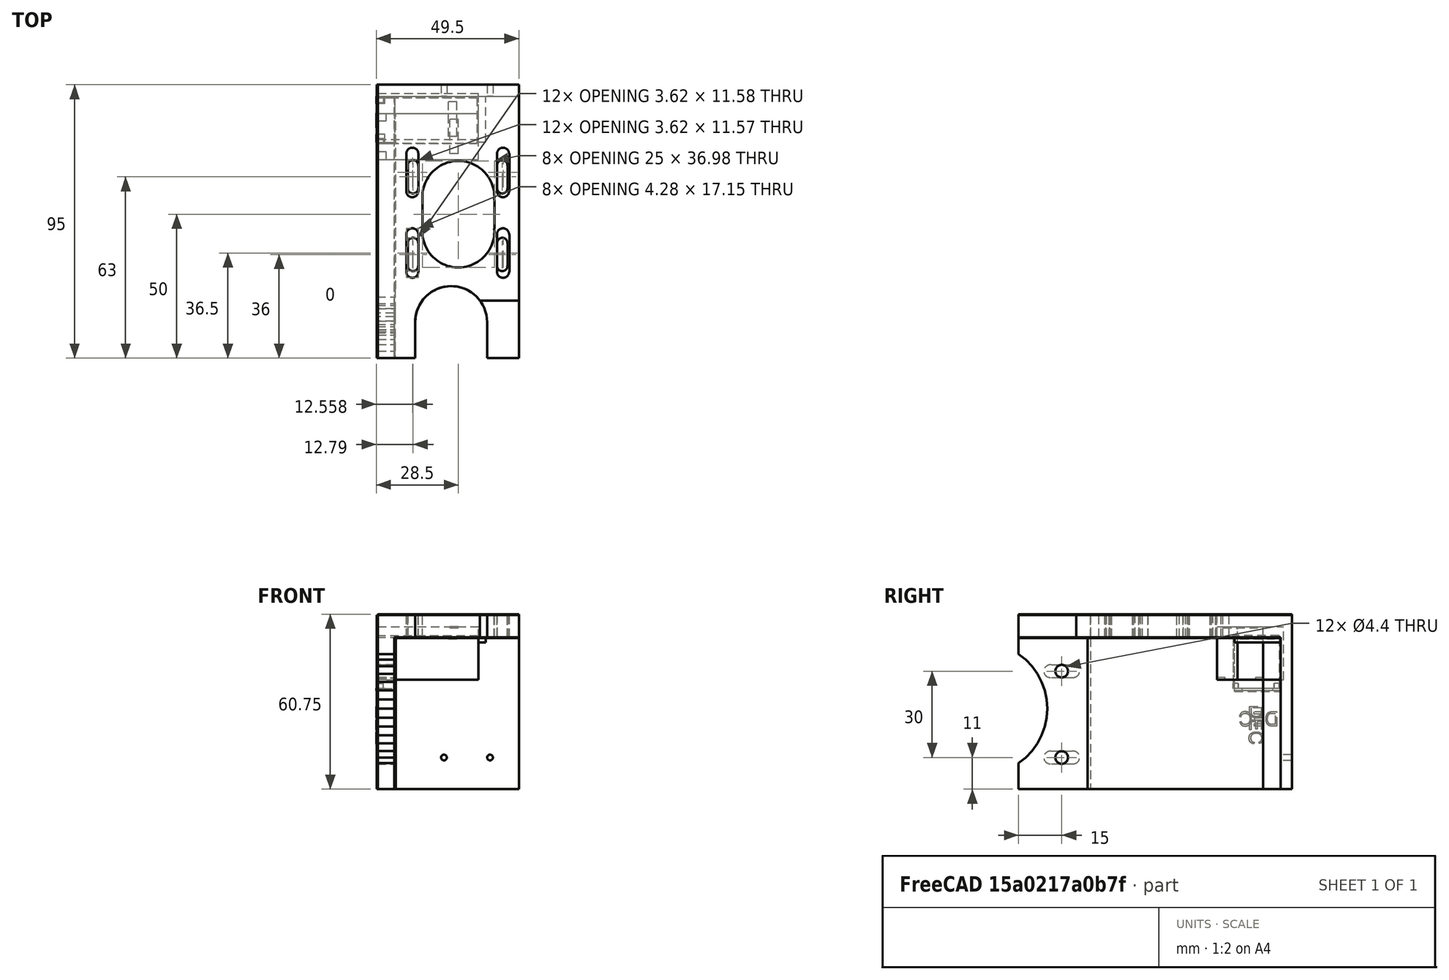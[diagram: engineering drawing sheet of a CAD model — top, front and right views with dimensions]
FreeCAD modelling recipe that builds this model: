
FCSTD DOCUMENT  (FreeCAD 0.17R11223 (Git))
Label: EQ motor V3 fin
License: All rights reserved
LicenseURL: http://en.wikipedia.org/wiki/All_rights_reserved
objects: Part::Feature×18, Part::Box×15, Part::Cut×13, Part::MultiFuse×8, Part::Cylinder×8, Part::Extrusion×3, Part::Part2DObjectPython×1
note: 66 computed .brp shape members not serialized (recipe doc carries the construction recipe); baked Part::Feature solids carry a one-line shape summary decoded from their .brp

FEATURE [Part::Feature] Cut026_solid  label="zadni stena (Solid)"
  shape: bbox 49 x 4 x 60.5 mm, 8 faces (baked)
FEATURE [Part::Feature] Fusion008_solid  label="Boky"
  shape: bbox 49 x 85 x 60.5 mm, 76 faces (baked)
FEATURE [Part::Box] Box005009  label="Krychle009"
  AttacherType = Attacher::AttachEngine3D
  Height = 18.5
  Length = 35
  Placement = pos=(-5,75,-44) rot=(0,0,1;0rad)
  Width = 16
FEATURE [Part::Box] Box005011  label="Krychle010"
  AttacherType = Attacher::AttachEngine3D
  Height = 2.7
  Length = 3
  Placement = pos=(-5,75,-45.8) rot=(0,0,1;0rad)
  Width = 2.7
FEATURE [Part::Box] Box005012  label="Krychle011"
  AttacherType = Attacher::AttachEngine3D
  Height = 2.7
  Length = 3
  Placement = pos=(-5,88.4,-45.8) rot=(0,0,1;0rad)
  Width = 2.7
FEATURE [Part::Box] Box005014  label="Krychle013"
  AttacherType = Attacher::AttachEngine3D
  Height = 2
  Length = 3
  Placement = pos=(20,77,-26) rot=(0,0,1;0rad)
  Width = 12
FEATURE [Part::Box] Box005015  label="Pro RJ"
  AttacherType = Attacher::AttachEngine3D
  Height = 18.5
  Length = 35
  Placement = pos=(-5,82,-44) rot=(0,0,1;0rad)
  Width = 16
FEATURE [Part::Box] Box005016  label="Krychle014"
  AttacherType = Attacher::AttachEngine3D
  Height = 8
  Length = 49
  Placement = pos=(-5,91,-29.5) rot=(0,0,1;0rad)
  Width = 6
FEATURE [Part::Box] Box005017  label="Krychle015"
  AttacherType = Attacher::AttachEngine3D
  Height = 60
  Length = 6
  Placement = pos=(-5,91,-82) rot=(0,0,1;0rad)
  Width = 6
FEATURE [Part::MultiFuse] Fusion
  Shapes = -> [Box005017,Box005016,Cut026_solid,Fusion008_solid]
FEATURE [Part::Feature] Fusion_solid  label="Fusion (Solid)"
  shape: bbox 49 x 95 x 60.5 mm, 91 faces (baked)
FEATURE [Part::Feature] Fusion_solid001  label="Fusion (Solid)001"
  shape: bbox 49 x 95 x 60.5 mm, 72 faces (baked)
FEATURE [Part::Feature] Fusion_solid_cs  label="REZ A"
  shape: bbox 49 x 95 x 4e-07 mm, 0 faces, 0 solids (baked)
FEATURE [Part::Feature] Fusion_solid001_cs  label="REZ B"
  shape: bbox 5e-07 x 95 x 60.5 mm, 0 faces, 0 solids (baked)
FEATURE [Part::Feature] Cut026_solid001  label="zadni stena (Solid)001"
  shape: bbox 49 x 4 x 60.5 mm, 8 faces (baked)
FEATURE [Part::Extrusion] Extrude  label="Vrsek"
  Base = -> Fusion_solid_cs
  Dir = (0,0,1)
  DirMode = 2
  FaceMakerClass = Part::FaceMakerBullseye
  LengthFwd = 8
  LengthRev = 0
  Placement = pos=(0,0,-2.5) rot=(0,0,1;0rad)
  Solid = true
  Symmetric = false
FEATURE [Part::Extrusion] Extrude001  label="Bok"
  Base = -> Fusion_solid001_cs
  Dir = (1,0,0)
  DirMode = 2
  FaceMakerClass = Part::FaceMakerBullseye
  LengthFwd = 6
  LengthRev = 0
  Placement = pos=(-1.8,0,0) rot=(0,0,1;0rad)
  Solid = true
  Symmetric = false
FEATURE [Part::MultiFuse] Fusion001
  Shapes = -> [Cut026_solid001,Extrude,Extrude001]
FEATURE [Part::Feature] Fusion001001  label="Fusion002"
  shape: bbox 49.3 x 95 x 60.75 mm, 66 faces (baked)
FEATURE [Part::Feature] Fusion001001_solid  label="Drzak Bez RJ"
  shape: bbox 49.3 x 95 x 60.75 mm, 66 faces (baked)
FEATURE [Part::Box] Box005018  label="Krychle016"
  AttacherType = Attacher::AttachEngine3D
  Height = 18.5
  Length = 35
  Placement = pos=(-5.5,81,-47.75) rot=(0,0,1;0rad)
  Width = 16
FEATURE [Part::Cut] Cut
  Base = -> Box005009
  Tool = -> Box005011
FEATURE [Part::Cut] Cut001
  Base = -> Cut
  Tool = -> Box005012
FEATURE [Part::Cut] Cut002  label="Pro RJ001"
  Base = -> Cut001
  Tool = -> Box005014
FEATURE [Part::Feature] Cut002_solid  label="Pro RJ001 (Solid)"
  Placement = pos=(-0.5,6,-3.75) rot=(0,0,1;0rad)
  shape: bbox 35 x 16 x 18.5 mm, 17 faces (baked)
FEATURE [Part::MultiFuse] Fusion001002
  Shapes = -> [Fusion001001_solid,Box005018]
FEATURE [Part::Cut] Cut003
  Base = -> Fusion001002
  Tool = -> Cut002_solid
FEATURE [Part::Feature] Cut003001  label="Cut004"
  shape: bbox 49.5 x 95 x 60.75 mm, 85 faces (baked)
FEATURE [Part::Feature] Cut003001_solid  label="EQ motor V3"
  shape: bbox 49.5 x 95 x 60.75 mm, 85 faces (baked)
FEATURE [Part::Box] Box009  label="Doraz003"
  AttacherType = Attacher::AttachEngine3D
  Height = 2
  Length = 2.5
  Placement = pos=(30,81,-31) rot=(0,0,1;0rad)
  Width = 16
FEATURE [Part::Feature] Fusion001003001  label="DIRA 010"
  shape: bbox 8 x 12.4 x 4.5 mm, 10 faces (baked)
FEATURE [Part::Feature] Fusion001003002  label="DIRA 011"
  Placement = pos=(0,0,-30) rot=(0,0,1;0rad)
  shape: bbox 8 x 12.4 x 4.5 mm, 10 faces (baked)
FEATURE [Part::Feature] Cut005_solid002002005  label="RJ45 M DE002"
  Placement = pos=(53.5,165.5,-34) rot=(1,0,0;3.14159rad)
  shape: bbox 35 x 15.95 x 18.45 mm, 12 faces (baked)
FEATURE [Part::Box] Box  label="Krychle"
  AttacherType = Attacher::AttachEngine3D
  Height = 20
  Length = 6.05
  Placement = pos=(-5.2,81,-48) rot=(0,0,1;0rad)
  Width = 16
FEATURE [Part::MultiFuse] Fusion001003003
  Shapes = -> [Box009,Box,Cut003001_solid]
FEATURE [Part::Cut] Cut003002  label="RJ n"
  Base = -> Fusion001003003
  Tool = -> Cut005_solid002002005
FEATURE [Part::Cylinder] Cylinder  label="Válec"
  Angle = 360
  AttacherType = Attacher::AttachEngine3D
  Height = 10
  Radius = 2.1
FEATURE [Part::Cylinder] Cylinder001  label="Válec001"
  Angle = 360
  AttacherType = Attacher::AttachEngine3D
  Height = 10
  Placement = pos=(0,13,0) rot=(0,0,1;0rad)
  Radius = 2.1
FEATURE [Part::Box] Box005019  label="Krychle017"
  AttacherType = Attacher::AttachEngine3D
  Height = 10
  Length = 4.2
  Placement = pos=(-2,0,0) rot=(0,0,1;0rad)
  Width = 13
FEATURE [Part::MultiFuse] Fusion001003004  label="Dira M"
  Placement = pos=(7,36,-30) rot=(0,0,1;0rad)
  Shapes = -> [Cylinder,Cylinder001,Box005019]
FEATURE [Part::Cylinder] Cylinder002  label="Válec002"
  Angle = 360
  AttacherType = Attacher::AttachEngine3D
  Height = 10
  Radius = 2.1
FEATURE [Part::Cylinder] Cylinder003  label="Válec003"
  Angle = 360
  AttacherType = Attacher::AttachEngine3D
  Height = 10
  Placement = pos=(0,13,0) rot=(0,0,1;0rad)
  Radius = 2.1
FEATURE [Part::Box] Box005020  label="Krychle018"
  AttacherType = Attacher::AttachEngine3D
  Height = 10
  Length = 4.2
  Placement = pos=(-2,0,0) rot=(0,0,1;0rad)
  Width = 13
FEATURE [Part::MultiFuse] Fusion001003005  label="Dira M001"
  Placement = pos=(38.5,36,-30) rot=(0,0,1;0rad)
  Shapes = -> [Cylinder002,Cylinder003,Box005020]
FEATURE [Part::Cylinder] Cylinder004  label="Válec004"
  Angle = 360
  AttacherType = Attacher::AttachEngine3D
  Height = 10
  Radius = 2.1
FEATURE [Part::Cylinder] Cylinder005  label="Válec005"
  Angle = 360
  AttacherType = Attacher::AttachEngine3D
  Height = 10
  Placement = pos=(0,13,0) rot=(0,0,1;0rad)
  Radius = 2.1
FEATURE [Part::Box] Box005021  label="Krychle019"
  AttacherType = Attacher::AttachEngine3D
  Height = 10
  Length = 4.2
  Placement = pos=(-2,0,0) rot=(0,0,1;0rad)
  Width = 13
FEATURE [Part::MultiFuse] Fusion001003006  label="Dira M002"
  Placement = pos=(7,64,-30) rot=(0,0,1;0rad)
  Shapes = -> [Cylinder004,Cylinder005,Box005021]
FEATURE [Part::Cylinder] Cylinder006  label="Válec006"
  Angle = 360
  AttacherType = Attacher::AttachEngine3D
  Height = 10
  Radius = 2.1
FEATURE [Part::Cylinder] Cylinder007  label="Válec007"
  Angle = 360
  AttacherType = Attacher::AttachEngine3D
  Height = 10
  Placement = pos=(0,13,0) rot=(0,0,1;0rad)
  Radius = 2.1
FEATURE [Part::Box] Box005022  label="Krychle020"
  AttacherType = Attacher::AttachEngine3D
  Height = 10
  Length = 4.2
  Placement = pos=(-2,0,0) rot=(0,0,1;0rad)
  Width = 13
FEATURE [Part::MultiFuse] Fusion001003007  label="Dira M003"
  Placement = pos=(38.5,64,-30) rot=(0,0,1;0rad)
  Shapes = -> [Cylinder006,Cylinder007,Box005022]
FEATURE [Part::Cut] Cut003003
  Base = -> Cut003002
  Tool = -> Fusion001003001
FEATURE [Part::Cut] Cut003004
  Base = -> Cut003003
  Tool = -> Fusion001003002
FEATURE [Part::Cut] Cut003005
  Base = -> Cut003004
  Tool = -> Fusion001003004
FEATURE [Part::Cut] Cut003006
  Base = -> Cut003005
  Tool = -> Fusion001003005
FEATURE [Part::Cut] Cut003007
  Base = -> Cut003006
  Tool = -> Fusion001003006
FEATURE [Part::Cut] Cut003008  label="DEC  F2"
  Base = -> Cut003007
  Tool = -> Fusion001003007
FEATURE [Part::Box] Box005023  label="Krychle021"
  AttacherType = Attacher::AttachEngine3D
  Height = 10
  Length = 16
  Placement = pos=(30,5,-31) rot=(0,0,1;0rad)
  Width = 21
FEATURE [Part::Cut] Cut003009
  Base = -> Cut003008
  Tool = -> Box005023
FEATURE [Part::Feature] Cut003009001  label="Cut003010"
  shape: bbox 49.5 x 95 x 60.75 mm, 121 faces (baked)
FEATURE [Part::Part2DObjectPython] ShapeString  # Draft 2D object (typed FeaturePython)
  FontFile = Z:/A8 ZS/FREECAD/ARIAL.TTF
  Placement = pos=(-5.3,89.1913,-58.4092) rot=(0,0,1;0rad)
  Size = 5
  String = DEC
  Tracking = 0
FEATURE [Part::Extrusion] Extrude002
  Base = -> ShapeString
  Dir = (0,0,1)
  DirMode = 2
  FaceMakerClass = Part::FaceMakerBullseye
  LengthFwd = 0.5
  LengthRev = 0
  Placement = pos=(53,-3,-58) rot=(0,1,0;1.5708rad)
  Solid = false
  Symmetric = false
FEATURE [Part::Feature] Extrude002001  label="Extrude003"
  Placement = pos=(0,149,31) rot=(-1,0,0;1.5708rad)
  shape: bbox 0.5 x 13.04 x 5.028 mm, 62 faces, 3 solids (baked)
  expr: Placement.Base.x = 0
FEATURE [Part::Cut] Cut003009002
  Base = -> Cut003009001
  Tool = -> Extrude002001
FEATURE [Part::Feature] Cut003009002001  label="DEC MOTOR HOLDER"
  shape: bbox 49.5 x 95 x 60.75 mm, 181 faces (baked)
